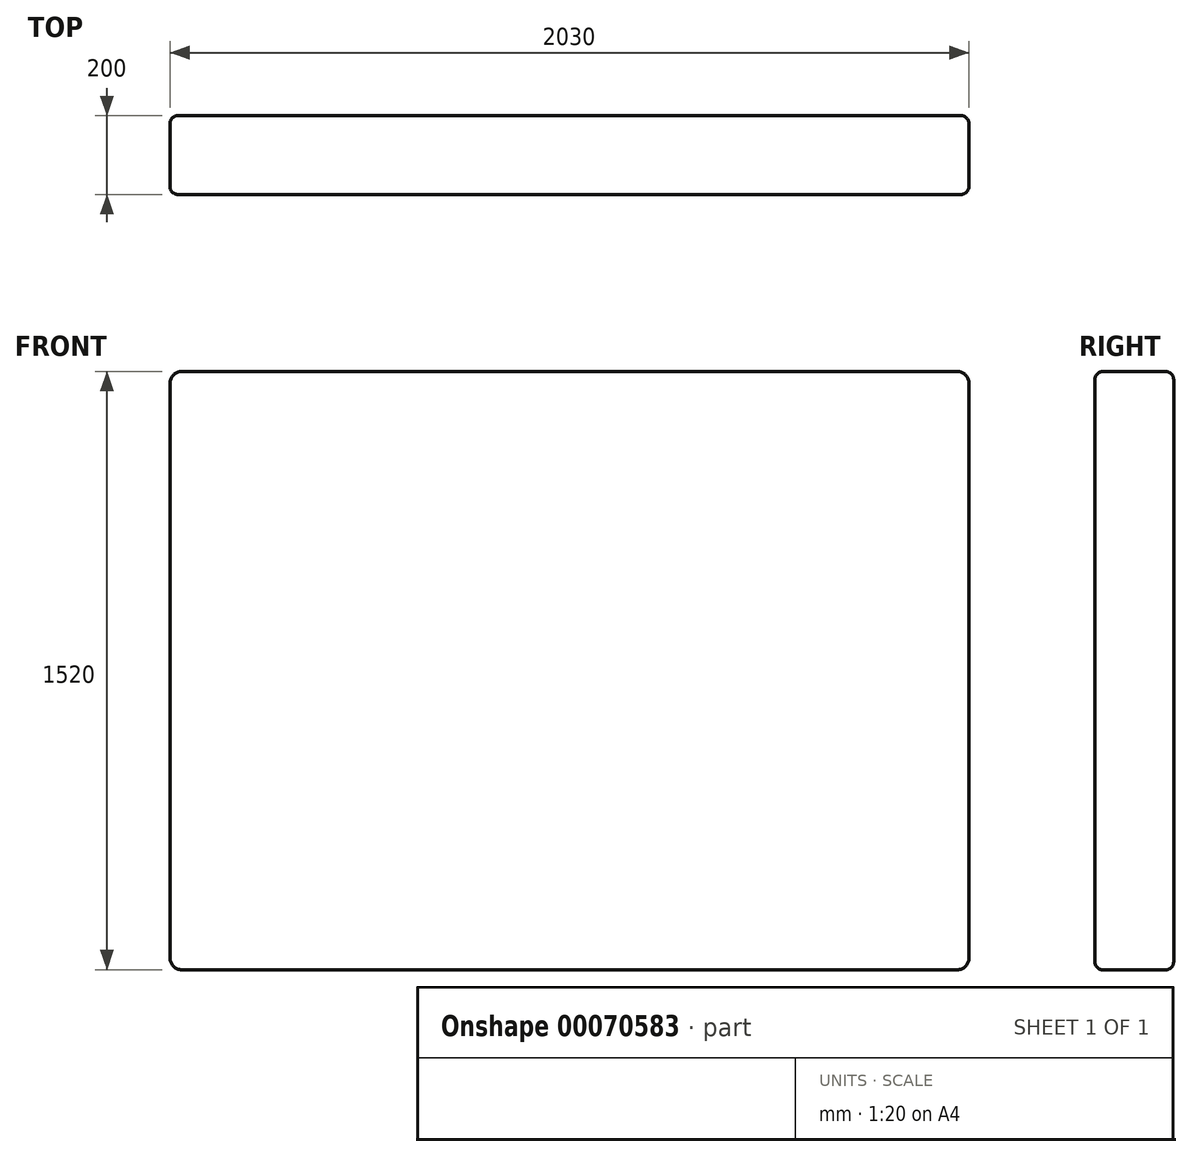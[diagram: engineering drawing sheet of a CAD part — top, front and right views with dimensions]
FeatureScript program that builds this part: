
annotation { "Feature Type Name" : "Feature", "Feature Type Description" : "" }
export const myFeature = defineFeature(function(context is Context, id is Id, definition is map)
    precondition{}
    {
        {
            var Q0;
            Q0=qCreatedBy(makeId("Front.planeOp"),FACE);
            var sketch = newSketch(context, id + "F0", { "sketchPlane" : qUnion([Q0])});
            skLineSegment(sketch, "E0.bottom", {"start": v(0, 0) * mm, "end": v(2030, 0) * mm});
            skLineSegment(sketch, "E0.top", {"start": v(0, 1520) * mm, "end": v(2030, 1520) * mm});
            skLineSegment(sketch, "E0.left", {"start": v(0, 0) * mm, "end": v(0, 1520) * mm});
            skLineSegment(sketch, "E0.right", {"start": v(2030, 0) * mm, "end": v(2030, 1520) * mm});
            skSolve(sketch);
        }
        {
            var Q0;
            Q0=makeQuery(id+"F0.imprint","IMPRINT",FACE,{"disambiguationData":[TD([[makeQuery(id+"F0.imprint","IMPRINT",EDGE,{"derivedFrom":sQuery(id+"F0.wireOp",EDGE,"E0.bottom")}),1.0]])]});
            extrude(context, id + "F1", {"entities" : qUnion([Q0]), "depth" : 200 * mm});
        }
        {
            var Q0;
            Q0=makeQuery(id+"F1.opExtrude","SWEPT_EDGE",EDGE,{"disambiguationData":[OSD([sQuery(id+"F0.wireOp",EDGE,"E0.bottom"),sQuery(id+"F0.wireOp",EDGE,"E0.right")])]});
            var Q1;
            Q1=makeQuery(id+"F1.opExtrude","SWEPT_EDGE",EDGE,{"disambiguationData":[OSD([sQuery(id+"F0.wireOp",EDGE,"E0.bottom"),sQuery(id+"F0.wireOp",EDGE,"E0.left")])]});
            var Q2;
            Q2=makeQuery(id+"F1.opExtrude","SWEPT_EDGE",EDGE,{"disambiguationData":[OSD([sQuery(id+"F0.wireOp",EDGE,"E0.top"),sQuery(id+"F0.wireOp",EDGE,"E0.right")])]});
            var Q3;
            Q3=makeQuery(id+"F1.opExtrude","SWEPT_EDGE",EDGE,{"disambiguationData":[OSD([sQuery(id+"F0.wireOp",EDGE,"E0.top"),sQuery(id+"F0.wireOp",EDGE,"E0.left")])]});
            fillet(context, id + "F2", {"entities" : qUnion([Q0, Q1, Q2, Q3]), "radius" : 30 * mm, "tangentPropagation" : true, "allowEdgeOverflow" : false});
        }
        {
            var Q0;
            Q0=makeQuery(id+"F1.opExtrude","CAP_EDGE",EDGE,{"disambiguationData":[OSD([sQuery(id+"F0.wireOp",EDGE,"E0.bottom")])],"isStart":false});
            var Q1;
            Q1=makeQuery(id+"F1.opExtrude","CAP_EDGE",EDGE,{"disambiguationData":[OSD([sQuery(id+"F0.wireOp",EDGE,"E0.bottom")])],"isStart":true});
            fillet(context, id + "F3", {"entities" : qUnion([Q0, Q1]), "radius" : 20 * mm, "tangentPropagation" : true, "allowEdgeOverflow" : false});
        }
    });
